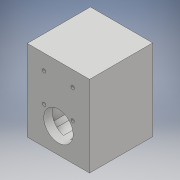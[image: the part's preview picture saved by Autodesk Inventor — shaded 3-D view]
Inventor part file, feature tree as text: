
AUTODESK INVENTOR PART (.ipt)
format: ipt  version: 2018 (Build 220112000, 112)  size: 430,592 bytes
history: native  units: mm
features: sketch x20, projected_geometry x18, extrude x17, hole x3, fillet x3, chamfer x1, mirror x1
ambient origin geometry x8: Origin, YZ Plane, XZ Plane, XY Plane, X Axis, Y Axis, Z Axis, Center Point
bodies: Solid1 (feature_tree)
feature tree (63):
  extrude  "Extrusion1"  Depth=45.0mm
  extrude  "Extrusion2"  Depth=1.95mm
  hole  "Hole1"  [1 undecoded]
  hole  "Hole2"  [1 undecoded]
  fillet  "Fillet1"  Radius=14.0mm
  extrude  "Extrusion3"  Depth=18.5mm
  extrude  "Extrusion4"  Depth=10.0mm
  extrude  "Extrusion5"  Depth=2.195mm
  extrude  "Extrusion6"  Depth=20.5mm
  hole  "Hole3"  [1 undecoded]
  extrude  "Extrusion7"  Depth=0.5mm
  extrude  "Extrusion8"  Depth=5.0mm TaperAngle=0.0deg
  extrude  "Extrusion9"  Depth=10.0mm
  extrude  "Extrusion10"  Depth=10.0mm
  extrude  "Extrusion11"  Depth=14.5mm
  extrude  "Extrusion12"  Depth=14.5mm
  extrude  "Extrusion13"  Depth=5.0mm
  extrude  "Extrusion14"  Depth=5.0mm
  extrude  "Extrusion15"  Depth=5.0mm
  extrude  "Extrusion16"  Depth=5.0mm
  extrude  "Extrusion17"  Depth=9.0mm
  chamfer  "Chamfer1"  Distance=14.75mm
  fillet  "Fillet7"  Radius=4.0mm
  fillet  "Fillet8"  Radius=1.0mm
  mirror  "Mirror1"
  sketch  "Sketch1"  dims[d0=24.5mm d1=45.0mm]
  sketch  "Sketch2"  dims[d2=1.95mm d3=0.0mm d4=2.25mm]
  projected_geometry  "Projected Loop1"
  sketch  "Sketch3"  dims[d5=20.0mm d6=2.25mm]
  projected_geometry  "Projected Loop2"
  sketch  "Sketch4"  dims[d7=5.25mm d8=5.25mm d9=14.0mm]
  projected_geometry  "Projected Loop3"
  sketch  "Sketch5"  dims[d10=5.25mm d11=18.5mm]
  projected_geometry  "Projected Loop4"
  sketch  "Sketch6"  dims[d12=10.0mm d13=0.0mm d14=20.5mm]
  projected_geometry  "Projected Loop5"
  sketch  "Sketch7"  dims[d15=2.0mm d16=2.195mm]
  projected_geometry  "Projected Loop6"
  sketch  "Sketch8"  dims[d17=2.0mm]
  projected_geometry  "Projected Loop7"
  sketch  "Sketch9"  dims[d18=2.4mm d19=6.0mm d20=4.4mm d21=2.0mm d22=90.0deg d23=8.0mm d24=20.594885mm d25=20.5mm]
  projected_geometry  "Projected Loop8"
  projected_geometry  "Projected Loop9"
  sketch  "Sketch10"  dims[d26=26.65mm d27=2.0mm]
  projected_geometry  "Projected Loop10"
  projected_geometry  "Projected Loop11"
  sketch  "Sketch11"  dims[d28=2.0mm]
  projected_geometry  "Projected Loop12"
  sketch  "Sketch12"  dims[d29=2.4mm d30=6.0mm d31=4.4mm d32=2.0mm d33=90.0deg d34=8.0mm d35=20.594885mm d36=0.5mm]
  sketch  "Sketch13"  dims[d37=18.0mm d38=5.0mm d39=0.0mm]
  sketch  "Sketch14"  dims[d41=10.0mm d42=0.0mm d43=24.5mm]
  projected_geometry  "Projected Loop13"
  sketch  "Sketch15"  dims[d44=1.15mm d45=0.0mm d46=10.0mm]
  sketch  "Sketch16"  dims[d47=21.0mm d48=14.5mm]
  projected_geometry  "Projected Loop14"
  sketch  "Sketch17"  dims[d49=20.0mm d50=14.5mm]
  projected_geometry  "Projected Loop15"
  sketch  "Sketch18"  dims[d51=24.5mm d52=5.0mm]
  projected_geometry  "Projected Loop16"
  sketch  "Sketch19"  dims[d53=5.0mm d54=2.25mm]
  projected_geometry  "Projected Loop17"
  sketch  "Sketch20"  dims[d55=2.25mm d56=5.0mm d57=5.0mm d58=9.0mm d59=14.75mm d60=4.0mm d61=1.0mm d62=0.0mm d63=20.7mm d64=2.4mm d65=6.0mm d66=4.4mm d67=2.0mm d68=90.0deg d69=8.0mm d70=20.594885mm d72=32.0mm d73=5.0mm d74=0.0mm d75=1.0mm d76=0.0mm d77=12.25mm d78=0.0mm d80=8.0mm d81=4.5mm d82=0.0mm d84=0.2mm d85=0.0mm d86=21.0mm d87=0.5mm d88=0.0mm d91=8.0mm d92=0.0mm d93=5.0mm d94=0.0mm d95=5.0mm d96=0.0mm d98=0.2mm d99=0.0mm d100=0.2mm d101=0.0mm d102=2.5mm d103=2.0mm d104=45.0deg d105=1.5mm d114=0.5mm]
  projected_geometry  "Projected Loop18"
note: 3 required parameter values undecoded (feature->parameter linkage not recoverable at this tier; creation-order binding heuristic only, values carry confidence <= 0.55)
